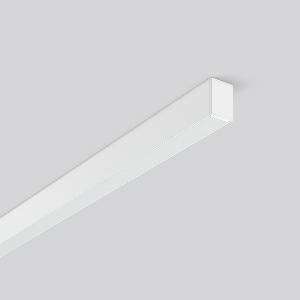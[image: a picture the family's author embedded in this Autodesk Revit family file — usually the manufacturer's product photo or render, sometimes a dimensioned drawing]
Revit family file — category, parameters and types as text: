
# Revit family: less_is_more_27_312200_002_1_76_3bb9
name_source: partatom
category: Lighting Fixtures
units: mm (PartAtom-declared; Revit-internal decimal feet)

## family parameters
Cut with Voids When Loaded = No
Host = Face
Light Source = No
Part Type = Normal
Room Calculation Point = No
Round Connector Dimension = Use Diameter
Shared = No

## types (1)
- LESS IS MORE 27 (1 x LED Modul 840, 2900 lm, 4000)
    Apparent Load = 39 VA
    CIE Flux Codes = 48 79 96 100 100
    Color Rendering = 80
    Color Temperature = 4000
    Default Elevation = 1800 mm
    Description = Series: LESS IS MORE 27
Ceiling and wall luminaire with slim design. Housing: extruded aluminium profile, powder-coated. End cap aluminium powder-coated. Diffuser made of non-yellowing plastic (PMMA), opal. Suitable for Ceiling mounting, Wall (surface). External driver with connecting cable. 
Colour: traffic white, matt (RAL 9016)
Length: 1512 mm
Width: 28 mm
Height: 38 mm
Lamp: LED
Socket: without socket
Colour temperature: 4000K
Colour rendering index (CRI): 82
System power: 39 W
Rated luminous flux: 2900 lm
Luminous efficiency: 74 lm/W
Control gear: Voltage converter, DALI dim.
Protection class: II
Type of protection: IP 20
    Height = 38 mm
    Lamp = 1 x LED Modul 840
    Lamp Light Flux = 2900 lm
    Lamp count = 1
    Length = 1512 mm
    Lifetime = 50000 h
    Luminous efficacy = 74 lm/W
    Manufacturer = RZB
    ModVariant = No
    Model = 312200.002.1.76
    Mounting Place = Ceiling, Wall
    Mounting Type = Surface mounted
    Number of Poles = 1
    OnlyDefault = Yes
    Power Factor = 1
    Product Name = LESS IS MORE 27
    Product group = Surface mounted LED linear luminaires
    ProductGroupID = 307
    Protection Class = Protection class II
    Protection Degree = IP 20
    RLX_Detail_Level = 1
    RLX_Emergency_Light_Flux = 0 lm
    RLX_Emergency_Type = 0
    RLX_Emergency_Type_DB = No
    RlxData = <blob elided: 22837 chars, md5=ef1b1cf8>
    Socket = socket
    Standby Power = 0 W
    System Light Flux = 2900 lm
    System Power = 39 W
    Type Comments = Product without accessories
    Type Image = 312196.002.jpg
    URL = http://relux.com
    VarID = ---
    Voltage = 230 V
    Voltage Range = 220-240 V
    Weight = 0.00 kg
    Width = 28 mm

## geometry (parser evidence)
native form markers: Blend x4, Sweep x11
no freeform markers — native parametric forms only
